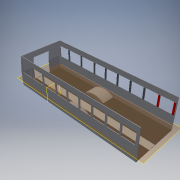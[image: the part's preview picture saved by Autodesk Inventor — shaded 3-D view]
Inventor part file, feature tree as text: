
AUTODESK INVENTOR PART (.ipt)
format: ipt  version: 2018.2 (Build 222227000, 227)  size: 540,160 bytes
history: native  units: in
note: dims shown in document units (in); Inventor stores cm internally (conversion verified against a paired STEP export)
features: extrude x47, sketch x14, plane x2, projected_geometry x2
ambient origin geometry x8: Origin, YZ Plane, XZ Plane, XY Plane, X Axis, Y Axis, Z Axis, Center Point
bodies: Solid1 (feature_tree)
feature tree (65):
  extrude  "Extrusion1"  Depth=92.5in
  extrude  "Extrusion2"  Depth=1.0in
  sketch  "Sketch3"  dims[d5=64.75in d6=0.0in d7=28.25in]
  extrude  "Extrusion3"  Depth=28.25in
  extrude  "Extrusion4"  Depth=64.75in TaperAngle=0.0deg
  sketch  "Sketch5"  dims[d9=1.0in d10=64.75in d11=0.0in]
  extrude  "Extrusion6"  Depth=6.5in
  extrude  "Extrusion7"  Depth=24.5in
  extrude  "Extrusion8"  Depth=3.5in
  extrude  "Extrusion9"  Depth=3.5in
  extrude  "Extrusion10"  Depth=3.5in
  extrude  "Extrusion11"  Depth=3.5in
  extrude  "Extrusion12"  Depth=3.5in
  extrude  "Extrusion13"  Depth=3.5in
  extrude  "Extrusion14"  Depth=3.5in
  sketch  "Sketch6"  dims[d12=64.75in d13=0.0in d16=6.5in]
  extrude  "Extrusion15"  Depth=3.75in
  extrude  "Extrusion16"  Depth=24.0in
  extrude  "Extrusion17"  Depth=3.75in
  extrude  "Extrusion18"  Depth=1.0in TaperAngle=0.0deg
  extrude  "Extrusion19"  Depth=1.0in TaperAngle=0.0deg
  extrude  "Extrusion20"  Depth=1.0in TaperAngle=0.0deg
  extrude  "Extrusion21"  Depth=1.0in TaperAngle=0.0deg
  extrude  "Extrusion22"  Depth=1.0in TaperAngle=0.0deg
  extrude  "Extrusion23"  Depth=1.0in TaperAngle=0.0deg
  sketch  "Sketch7"  dims[d17=29.5in d18=24.5in]
  extrude  "Extrusion24"  Depth=1.0in TaperAngle=0.0deg
  extrude  "Extrusion25"  Depth=1.0in TaperAngle=0.0deg
  extrude  "Extrusion26"  Depth=1.0in TaperAngle=0.0deg
  extrude  "Extrusion27"  Depth=3.75in
  extrude  "Extrusion28"  Depth=0.25in TaperAngle=0.0deg
  extrude  "Extrusion29"  Depth=0.25in TaperAngle=0.0deg
  extrude  "Extrusion30"  Depth=0.25in TaperAngle=0.0deg
  extrude  "Extrusion31"  Depth=0.25in TaperAngle=0.0deg
  extrude  "Extrusion32"  Depth=0.25in TaperAngle=0.0deg
  sketch  "Sketch8"  dims[d19=23.75in d20=3.5in]
  extrude  "Extrusion33"  Depth=0.25in TaperAngle=0.0deg
  extrude  "Extrusion34"  Depth=0.25in TaperAngle=0.0deg
  extrude  "Extrusion35"  Depth=0.25in TaperAngle=0.0deg
  extrude  "Extrusion36"  Depth=0.25in TaperAngle=0.0deg
  extrude  "Extrusion37"  Depth=1.0in TaperAngle=0.0deg
  extrude  "Extrusion38"  Depth=1.0in TaperAngle=0.0deg
  extrude  "Extrusion39"  Depth=1.0in TaperAngle=0.0deg
  extrude  "Extrusion40"  Depth=1.0in TaperAngle=0.0deg
  extrude  "Extrusion41"  Depth=1.0in TaperAngle=0.0deg
  extrude  "Extrusion42"  Depth=1.0in TaperAngle=0.0deg
  extrude  "Extrusion43"  Depth=1.0in TaperAngle=0.0deg
  extrude  "Extrusion44"  Depth=1.0in TaperAngle=0.0deg
  extrude  "Extrusion45"  Depth=1.0in TaperAngle=0.0deg
  plane  "Work Plane1"
  extrude  "Extrusion46"  Depth=0.25in TaperAngle=0.0deg
  plane  "Work Plane2"
  extrude  "Extrusion47"  Depth=3.5in
  extrude  "Extrusion48"  Depth=0.25in TaperAngle=0.0deg
  sketch  "Sketch1"  dims[d0=275.0in d1=92.5in]
  sketch  "Sketch2"  dims[d2=1.0in d3=0.0in d4=1.0in]
  projected_geometry  "Projected Loop1"
  projected_geometry  "Projected Loop3"
  sketch  "Sketch9"  dims[d21=31.5in d22=3.5in]
  sketch  "Sketch10"  dims[d24=31.5in d25=3.5in]
  sketch  "Sketch11"  dims[d26=24.5in d27=3.5in]
  sketch  "Sketch12"  dims[d28=24.5in d29=3.5in]
  sketch  "Sketch13"  dims[d30=24.5in d31=3.5in]
  sketch  "Sketch14"  dims[d32=24.5in d33=3.5in]
  sketch  "Sketch15"  dims[d35=24.5in d36=3.75in d37=24.0in d38=3.75in d39=1.0in d40=0.0in d41=1.0in d42=0.0in d43=1.0in d44=0.0in d45=1.0in d46=0.0in d47=1.0in d48=0.0in d49=1.0in d50=0.0in d51=1.0in d52=0.0in d53=1.0in d54=0.0in d55=1.0in d56=0.0in d57=3.75in d58=0.25in d59=0.0in d60=0.25in d61=0.0in d62=0.25in d63=0.0in d64=0.25in d65=0.0in d66=0.25in d67=0.0in d68=0.25in d69=0.0in d70=0.25in d71=0.0in d72=0.25in d73=0.0in d74=0.25in d75=0.0in d79=1.0in d80=0.0in d81=1.0in d82=0.0in d83=1.0in d84=0.0in d85=1.0in d86=0.0in d87=1.0in d88=0.0in d89=1.0in d90=0.0in d91=1.0in d92=0.0in d93=1.0in d94=0.0in d95=1.0in d96=0.0in d98=0.25in d99=0.0in d100=3.5in d101=0.25in d102=0.0in d103=0.25in d104=0.0in d105=0.25in d106=0.0in d107=0.25in d108=0.0in d109=0.25in d110=0.0in d111=0.25in d112=0.0in d113=0.25in d114=0.0in d115=0.25in d116=0.0in d117=104.5in d118=180.0deg d119=46.5in d121=26.0in d122=0.0in d123=104.5in d124=46.5in d126=26.0in d127=0.0in d128=30.25in d129=14.75in d130=0.001in d131=0.001in d132=0.0in d133=26.625in d134=50.75in d135=90.0deg d136=37.25in d137=13.3135in d138=0.0in d139=75.75in d142=8.375in d143=0.0in d144=10.375in d145=1.125in d146=0.25in d147=0.0in d148=1.125in d149=0.25in d150=0.0in]
